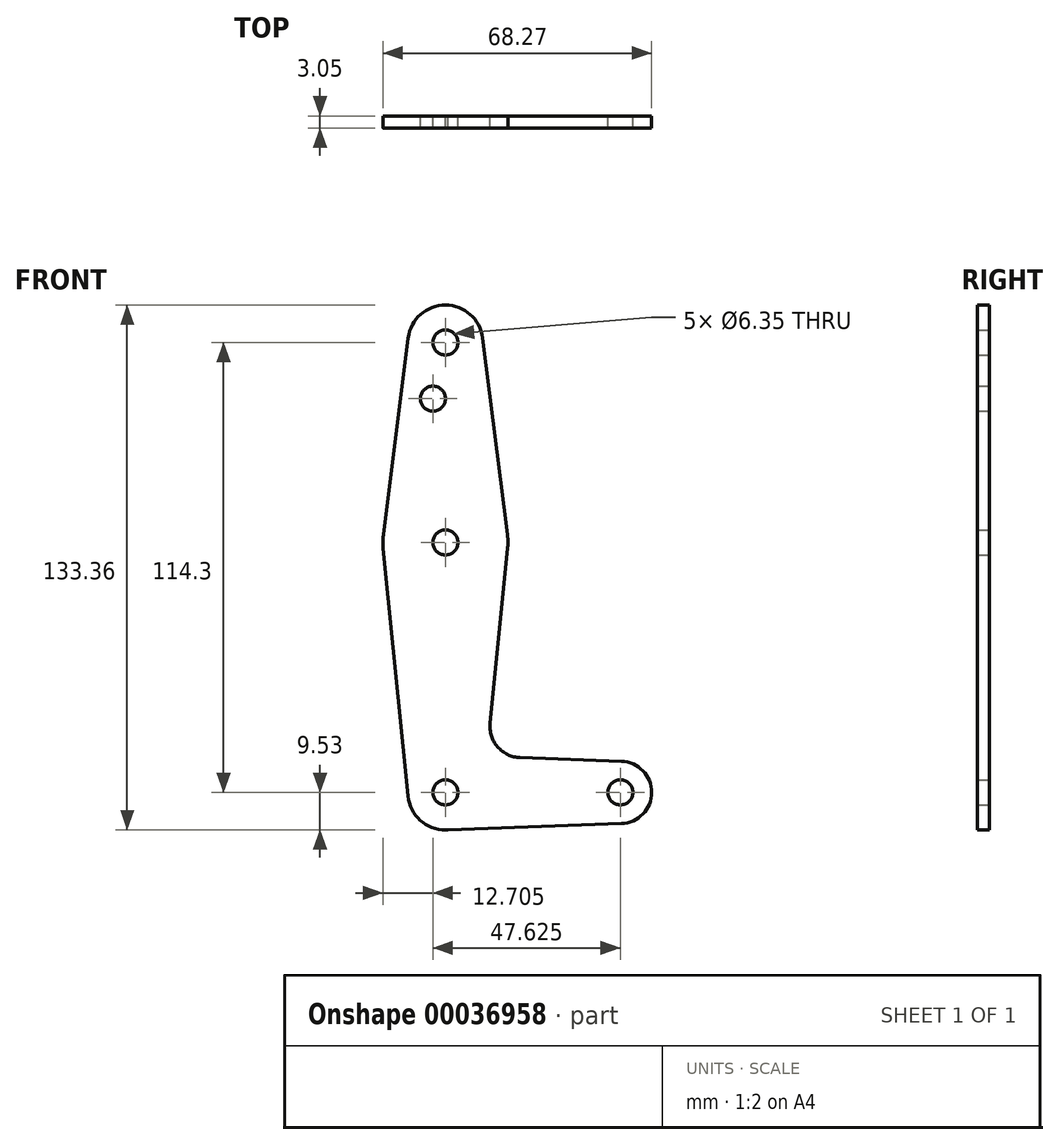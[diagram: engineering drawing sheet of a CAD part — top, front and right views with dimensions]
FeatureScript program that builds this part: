
annotation { "Feature Type Name" : "Feature", "Feature Type Description" : "" }
export const myFeature = defineFeature(function(context is Context, id is Id, definition is map)
    precondition{}
    {
        {
            var Q0;
            Q0=qCreatedBy(makeId("Front.planeOp"),FACE);
            var sketch = newSketch(context, id + "F0", { "sketchPlane" : qUnion([Q0])});
            skLineSegment(sketch, "E0", {"start": v(0, 114.3) * mm, "end": v(0, 0) * mm, "construction": true});
            skLineSegment(sketch, "E1", {"start": v(0, 0) * mm, "end": v(52.39, 0) * mm, "construction": true});
            skCircle(sketch, "E2", {"center": v(0, 114.3) * mm, "radius": 9.53 * mm});
            skCircle(sketch, "E3", {"center": v(0, 63.5) * mm, "radius": 15.88 * mm});
            skCircle(sketch, "E4", {"center": v(0, 0) * mm, "radius": 9.53 * mm});
            skCircle(sketch, "E5", {"center": v(44.45, 0) * mm, "radius": 7.94 * mm});
            skLineSegment(sketch, "E6", {"start": v(-9.45, 115.5) * mm, "end": v(-15.75, 65.48) * mm});
            skLineSegment(sketch, "E7", {"start": v(9.45, 115.5) * mm, "end": v(15.75, 65.48) * mm});
            skLineSegment(sketch, "E8", {"start": v(-15.8, 61.91) * mm, "end": v(-9.48, -0.95) * mm});
            skLineSegment(sketch, "E9", {"start": v(15.8, 61.91) * mm, "end": v(11.34, 17.59) * mm});
            skLineSegment(sketch, "E10", {"start": v(18.97, 8.85) * mm, "end": v(44.73, 7.93) * mm});
            skLineSegment(sketch, "E11", {"start": v(0, -9.53) * mm, "end": v(44.73, -7.93) * mm});
            skCircle(sketch, "E12", {"center": v(0, 114.3) * mm, "radius": 3.18 * mm});
            skCircle(sketch, "E13", {"center": v(-3.18, 100.03) * mm, "radius": 3.18 * mm});
            skCircle(sketch, "E14", {"center": v(0, 63.5) * mm, "radius": 3.18 * mm});
            skCircle(sketch, "E15", {"center": v(0, 0) * mm, "radius": 3.18 * mm});
            skCircle(sketch, "E16", {"center": v(44.45, 0) * mm, "radius": 3.18 * mm});
            skArc(sketch, "E17.filletArc", {"start": v(11.34, 17.59) * mm, "mid": v(13.26, 11.57) * mm, "end": v(18.97, 8.85) * mm});
            skSolve(sketch);
        }
        {
            var Q0;
            {var subQ1=sQuery(id+"F0.wireOp",EDGE,"E6");Q0=makeQuery(id+"F0.imprint","IMPRINT",FACE,{"disambiguationData":[TD([[makeQuery(id+"F0.imprint","IMPRINT",EDGE,{"derivedFrom":subQ1}),1.0]])]});}
            var Q1;
            Q1=makeQuery(id+"F0.imprint","IMPRINT",FACE,{"disambiguationData":[TD([[makeQuery(id+"F0.imprint","IMPRINT",EDGE,{"derivedFrom":sQuery(id+"F0.wireOp",EDGE,"E12")}),-1.0]])]});
            var Q2;
            Q2=makeQuery(id+"F0.imprint","IMPRINT",FACE,{"disambiguationData":[TD([[makeQuery(id+"F0.imprint","IMPRINT",EDGE,{"derivedFrom":sQuery(id+"F0.wireOp",EDGE,"E14")}),-1.0]])]});
            var Q3;
            {var subQ6=sQuery(id+"F0.wireOp",EDGE,"E8");Q3=makeQuery(id+"F0.imprint","IMPRINT",FACE,{"disambiguationData":[TD([[makeQuery(id+"F0.imprint","IMPRINT",EDGE,{"derivedFrom":subQ6}),1.0]])]});}
            var Q4;
            Q4=makeQuery(id+"F0.imprint","IMPRINT",FACE,{"disambiguationData":[TD([[makeQuery(id+"F0.imprint","IMPRINT",EDGE,{"derivedFrom":sQuery(id+"F0.wireOp",EDGE,"E15")}),-1.0]])]});
            var Q5;
            Q5=makeQuery(id+"F0.imprint","IMPRINT",FACE,{"disambiguationData":[TD([[makeQuery(id+"F0.imprint","IMPRINT",EDGE,{"derivedFrom":sQuery(id+"F0.wireOp",EDGE,"E16")}),-1.0]])]});
            extrude(context, id + "F1", {"entities" : qUnion([Q0, Q1, Q2, Q3, Q4, Q5]), "depth" : 3.05 * mm});
        }
        {
            var Q0;
            Q0 = qSketchRegion(id + "F0", true);
            extrude(context, id + "F2", {"entities" : qUnion([Q0]), "operationType" : NewBodyOperationType.ADD, "depth" : 3.05 * mm});
        }
        {
            var Q0;
            Q0 = qSketchRegion(id + "F0", true);
            extrude(context, id + "F3", {"entities" : qUnion([Q0]), "operationType" : NewBodyOperationType.ADD, "depth" : 3.05 * mm});
        }
    });
